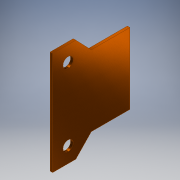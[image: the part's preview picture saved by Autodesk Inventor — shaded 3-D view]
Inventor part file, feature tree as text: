
AUTODESK INVENTOR PART (.ipt)
format: ipt  version: 2018.2 (Build 222227000, 227)  size: 139,264 bytes
history: native  units: mm
features: other x1, extrude x1, sketch x1
ambient origin geometry x8: Origin, YZ Plane, XZ Plane, XY Plane, X Axis, Y Axis, Z Axis, Center Point
bodies: Body1 (feature_tree)
feature tree (3):
  other  "Твердое тело1"
  extrude  "Выдавливание1"  Depth=40.0mm
  sketch  "Эскиз1"
